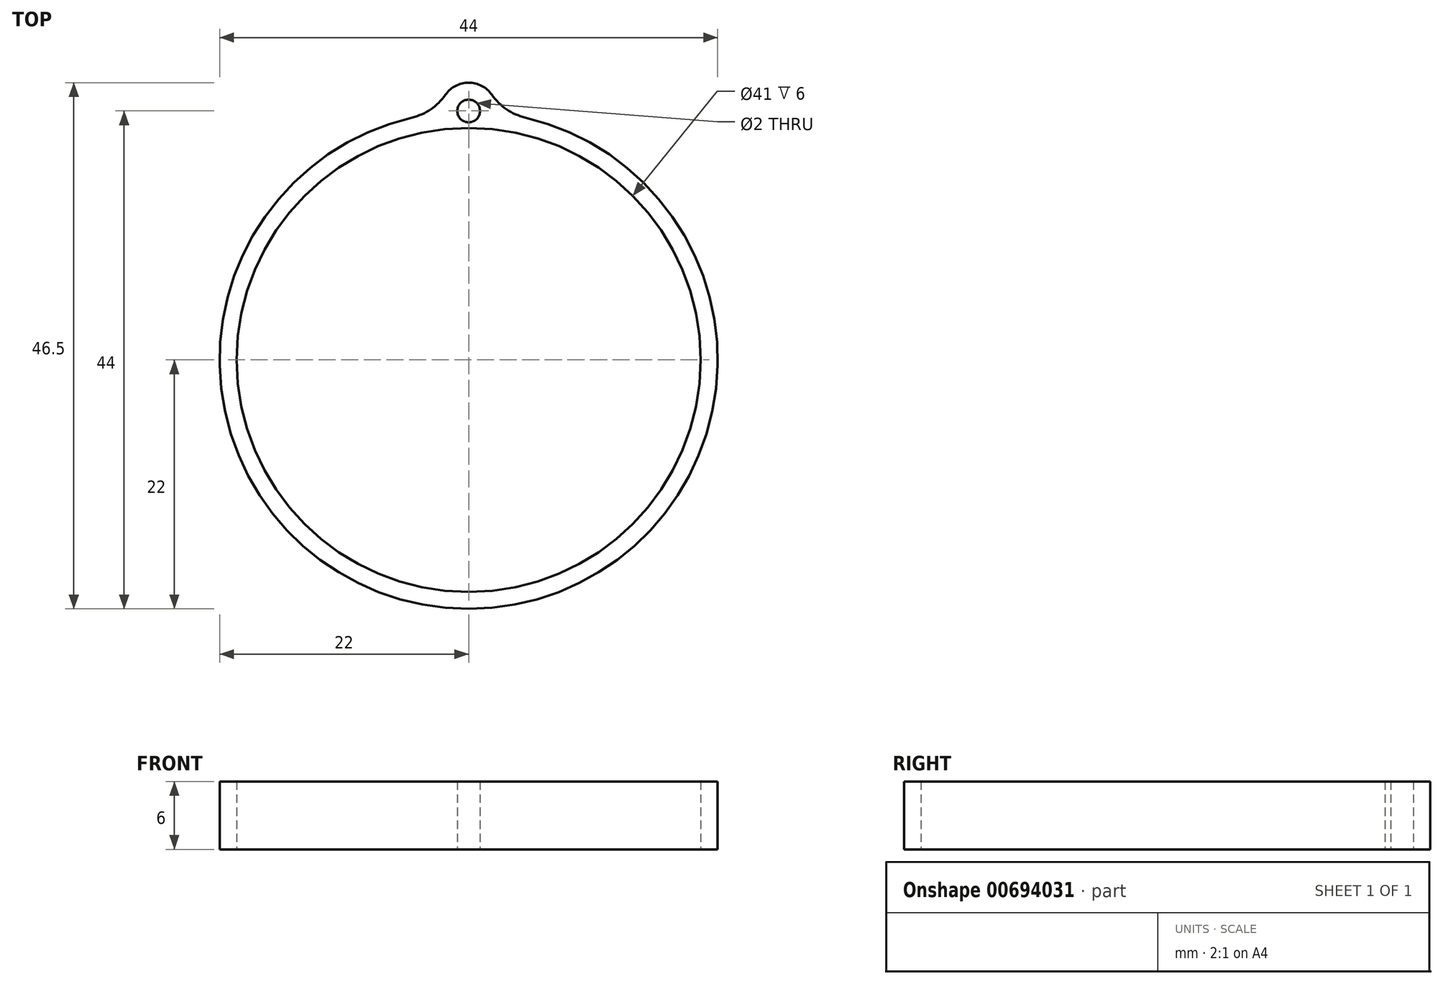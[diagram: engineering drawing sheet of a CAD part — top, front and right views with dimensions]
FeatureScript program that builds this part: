
annotation { "Feature Type Name" : "Feature", "Feature Type Description" : "" }
export const myFeature = defineFeature(function(context is Context, id is Id, definition is map)
    precondition{}
    {
        {
            var Q0;
            Q0=qCreatedBy(makeId("Top.planeOp"),FACE);
            var sketch = newSketch(context, id + "F0", { "sketchPlane" : qUnion([Q0])});
            skArc(sketch, "E0", {"start": v(-5.01, 21.42) * mm, "mid": v(0, -22) * mm, "end": v(5.01, 21.42) * mm});
            skCircle(sketch, "E1", {"center": v(0, 0) * mm, "radius": 20.5 * mm});
            skCircle(sketch, "E2", {"center": v(0, 22) * mm, "radius": 1 * mm});
            skArc(sketch, "E3", {"start": v(2.05, 23.43) * mm, "mid": v(0, 24.5) * mm, "end": v(-2.05, 23.43) * mm});
            skPoint(sketch, "E4.visualSharp", {"position": v(-2.5, 21.86) * mm});
            skArc(sketch, "E4.filletArc", {"start": v(-5.01, 21.42) * mm, "mid": v(-3.35, 22.15) * mm, "end": v(-2.05, 23.43) * mm});
            skPoint(sketch, "E5.visualSharp", {"position": v(2.5, 21.86) * mm});
            skArc(sketch, "E5.filletArc", {"start": v(2.05, 23.43) * mm, "mid": v(3.35, 22.15) * mm, "end": v(5.01, 21.42) * mm});
            skLineSegment(sketch, "E6", {"start": v(0, 22) * mm, "end": v(0, 20.5) * mm});
            skSolve(sketch);
        }
        {
            var Q0;
            Q0=makeQuery(id+"F0.imprint","IMPRINT",FACE,{"disambiguationData":[TD([[makeQuery(id+"F0.imprint","IMPRINT",EDGE,{"derivedFrom":sQuery(id+"F0.wireOp",EDGE,"E0")}),1.0]])]});
            extrude(context, id + "F1", {"entities" : qUnion([Q0]), "depth" : 6 * mm, "offsetDistance" : 25 * mm});
        }
    });
